# Revit family: Mechanism_Kit-Simon-500_CIMA
name_source: partatom
category: Electrical Fixtures
revit_build: Autodesk Revit 2014 (Build: 20130308_1515(x64)
units: mm (PartAtom-declared; Revit-internal decimal feet)

## types (6) — shared parameters
Current = 16 A
Default Elevation = 1219 mm
Manufacturer = SIMON
Protection against solid and liquid bodies = IP40
RJ45 compatibility figure = Keystone I, II and Systimax
Series = Simon 500 CIMA
Technical data sheet = http://www.simon.es
URL = http://www.simon.es
Voice and data connectors type = RJ45

## per-type parameters (varying)
| type | Box Type | Box depth | Cost | D3 | D4 | Description | Element Material | Frame Offset | Frame Type | Kit Material | Manufacturing material | Model | Overall dimensions | Protection against impacts | RAL Color | Width | e2 | e4 | n |
| 3 Modules, Surface wall | Electrical_Box-Surface-Simon-500_Cima : 3 Modules | 50 mm | 60.69€ | 63 mm | 126 mm | UPS workstation surface wall box kit with 1 double Schuko outlet, 1 double UPS Schuko outlet and 2 V&D plates for 1 RJ45 connector. | 9003 Signal white | 50 mm | Frame Connect | 9003 Signal white | Halogen-free thermoplastic to guarantee non-propagation of flames in the event of a fire | 51000302-030 | 223 x 167 mm | IK07 | 9003 Signal white | 220 mm | Null Connect | Double Data | 2 |
| 4 Modules, Surface wall | Electrical_Box-Surface-Simon-500_Cima : 4 Modules | 50 mm | 84.83€ | 126 mm | 189 mm | UPS workstation surface wall box kit with 2 double Schuko outlets, 1 double UPS Schuko outlet and 2 V&D plates for 2 RJ45 connectors. | 9003 Signal white | 50 mm | Frame Connect | 9003 Signal white | Halogen-free thermoplastic to guarantee non-propagation of flames in the event of a fire | 51000401-030 | 286 x 167 mm | IK07 | 9003 Signal white | 283 mm | Double Schuko | Double Data-Voice | 3 |
| 3 Modules, Flush mounting wall | Electrical_Box-Flush_Mounting-Simon-500_Cima : 3 Modules | 50 mm | 63.71€ | 63 mm | 126 mm | UPS workstation flush mounting wall box kit with 1 double Schuko outlet, 1 double UPS Schuko outlet and 2 V&D plates for 1 RJ45 connector. | 9003 Signal white | 0 mm | Frame Connect | 9003 Signal white | Halogen-free thermoplastic to guarantee non-propagation of flames in the event of a fire | 51000302-030 | 220 x 164 mm | IK07 | 9003 Signal white | 220 mm | Null Connect | Double Data | 2 |
| 4 Modules, Flush mounting wall | Electrical_Box-Flush_Mounting-Simon-500_Cima : 4 Modules | 50 mm | 88.06€ | 126 mm | 189 mm | UPS workstation flush mounting wall box kit with 2 double Schuko outlets, 1 double UPS Schuko outlet and 2 V&D plates for 2 RJ45 connectors. | 9003 Signal white | 0 mm | Frame Connect | 9003 Signal white | Halogen-free thermoplastic to guarantee non-propagation of flames in the event of a fire | 51000401-030 | 284 x 164 mm | IK07 | 9003 Signal white | 283 mm | Double Schuko | Double Data-Voice | 3 |
| 3 Modules, Flush mounting wall, Metal | Null Connect | 57 mm | 104.57€ | 63 mm | 126 mm | UPS workstation flush mounting metal wall box kit with 1 double Schuko outlet, 1 double UPS Schuko outlet and 2 V&D plates for 1 RJ45 connector. | Grey Finish | 0 mm | Frame Connect Metal | Stainless Steel, Brushed | Manufacturing material: Aluminium structure and stainless steel frame (AISI 430 ferritic stainless steel type) | 51002302-036 | 226 x 170 mm | IK10 |  | 226 mm | Null Connect | Double Data | 2 |
| 3 Modules, Surface wall, Metal | Null Connect | 50 mm | 60.69€ | 63 mm | 126 mm | UPS workstation surface metal wall box kit with 1 double Schuko outlet, 1 double UPS Schuko outlet and 2 V&D plates for 1 RJ45 connector. | Grey Finish | 57 mm | Frame Connect Metal Surface | Stainless Steel, Brushed | Aluminium structure and stainless steel frame (AISI 430 ferritic stainless steel type) | 51001302-036 | 223 x 167 mm | IK10 |  | 208 mm | Null Connect | Double Data | 2 |

## geometry (parser evidence)
native form markers: Blend x6
no freeform markers — native parametric forms only
